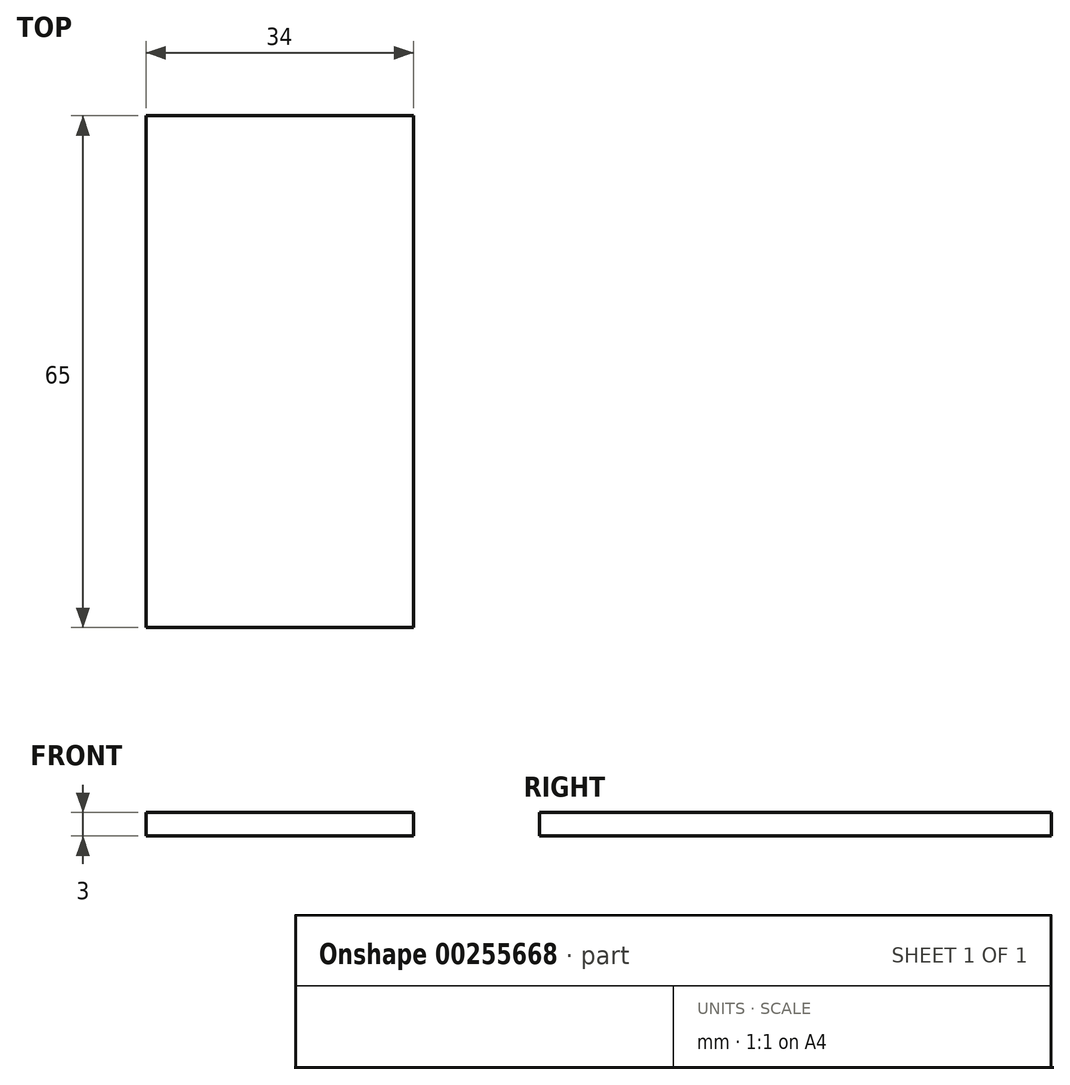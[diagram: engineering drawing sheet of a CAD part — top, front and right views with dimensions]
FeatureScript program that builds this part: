
annotation { "Feature Type Name" : "Feature", "Feature Type Description" : "" }
export const myFeature = defineFeature(function(context is Context, id is Id, definition is map)
    precondition{}
    {
        {
            var Q0;
            Q0=qCreatedBy(makeId("Top.planeOp"),FACE);
            var sketch = newSketch(context, id + "F0", { "sketchPlane" : qUnion([Q0])});
            skLineSegment(sketch, "E0.bottom", {"start": v(-17, -32.5) * mm, "end": v(17, -32.5) * mm});
            skLineSegment(sketch, "E0.top", {"start": v(-17, 32.5) * mm, "end": v(17, 32.5) * mm});
            skLineSegment(sketch, "E0.left", {"start": v(-17, -32.5) * mm, "end": v(-17, 32.5) * mm});
            skLineSegment(sketch, "E0.right", {"start": v(17, -32.5) * mm, "end": v(17, 32.5) * mm});
            skPoint(sketch, "E0.middle", {"position": v(0, 0) * mm});
            skSolve(sketch);
        }
        {
            var Q0;
            Q0 = qSketchRegion(id + "F0", true);
            extrude(context, id + "F1", {"entities" : qUnion([Q0]), "depth" : 3 * mm});
        }
    });
